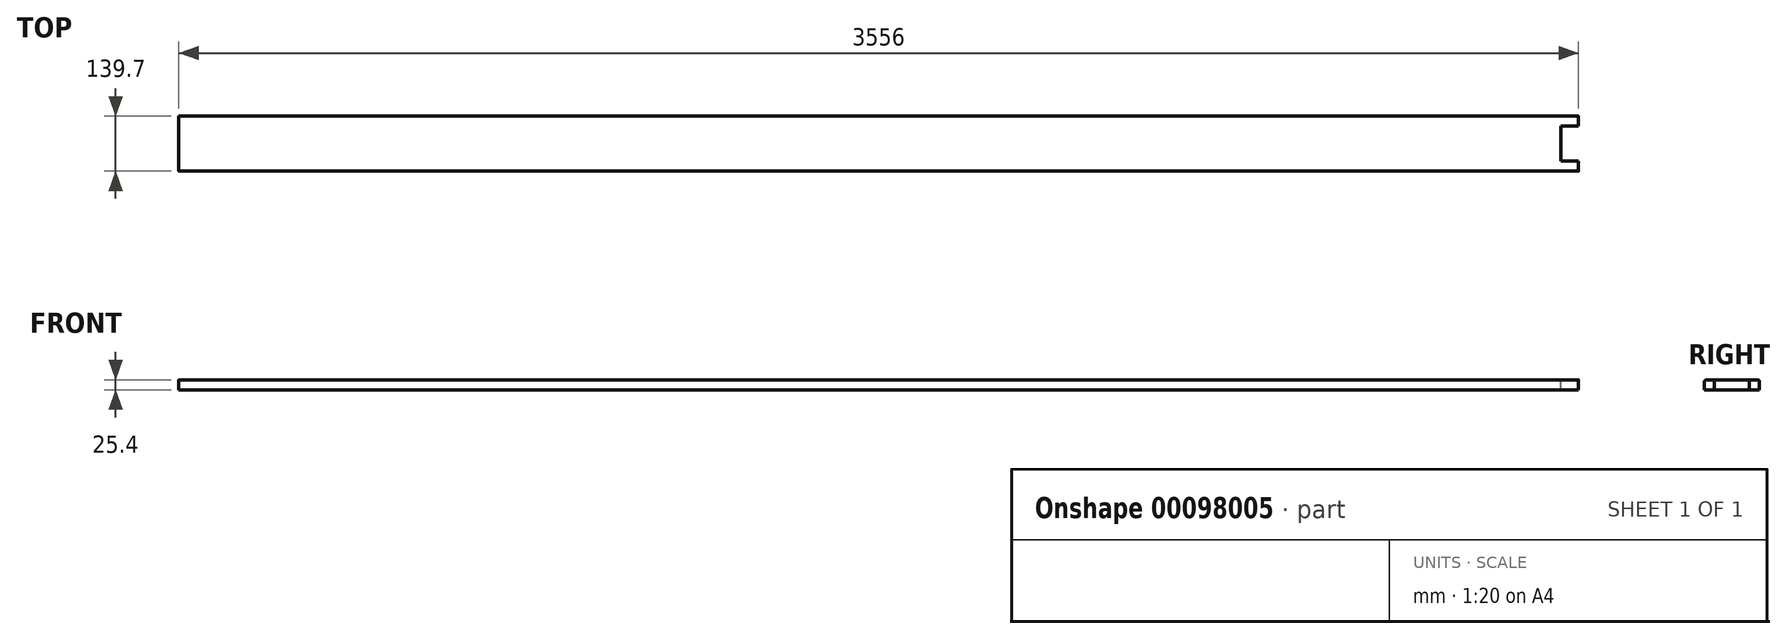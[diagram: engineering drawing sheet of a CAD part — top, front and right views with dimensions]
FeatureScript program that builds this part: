
annotation { "Feature Type Name" : "Feature", "Feature Type Description" : "" }
export const myFeature = defineFeature(function(context is Context, id is Id, definition is map)
    precondition{}
    {
        {
            var Q0;
            Q0=qCreatedBy(makeId("Top.planeOp"),FACE);
            var sketch = newSketch(context, id + "F0", { "sketchPlane" : qUnion([Q0])});
            skLineSegment(sketch, "E0.bottom", {"start": v(1778, 69.85) * mm, "end": v(-1778, 69.85) * mm});
            skLineSegment(sketch, "E0.top", {"start": v(1778, -69.85) * mm, "end": v(-1778, -69.85) * mm});
            skLineSegment(sketch, "E0.left", {"start": v(1778, 69.85) * mm, "end": v(1778, -69.85) * mm});
            skLineSegment(sketch, "E0.right", {"start": v(-1778, 69.85) * mm, "end": v(-1778, -69.85) * mm});
            skPoint(sketch, "E0.middle", {"position": v(0, 0) * mm});
            skSolve(sketch);
        }
        {
            var Q0;
            Q0=makeQuery(id+"F0.imprint","IMPRINT",FACE,{"disambiguationData":[TD([[makeQuery(id+"F0.imprint","IMPRINT",EDGE,{"derivedFrom":sQuery(id+"F0.wireOp",EDGE,"E0.bottom")}),1.0]])]});
            extrude(context, id + "F1", {"entities" : qUnion([Q0]), "depth" : 25.4 * mm});
        }
        {
            var Q0;
            Q0=makeQuery(id+"F1.opExtrude","CAP_FACE",FACE,{"disambiguationData":[OSD([sQuery(id+"F0.wireOp",EDGE,"E0.bottom"),sQuery(id+"F0.wireOp",EDGE,"E0.top"),sQuery(id+"F0.wireOp",EDGE,"E0.left"),sQuery(id+"F0.wireOp",EDGE,"E0.right")])],"isStart":false});
            var sketch = newSketch(context, id + "F2", { "sketchPlane" : qUnion([Q0])});
            skLineSegment(sketch, "E1", {"start": v(1778, 44.45) * mm, "end": v(1733.55, 44.45) * mm});
            skLineSegment(sketch, "E2", {"start": v(1733.55, 44.45) * mm, "end": v(1733.55, -44.45) * mm});
            skLineSegment(sketch, "E3", {"start": v(1733.55, -44.45) * mm, "end": v(1778, -44.45) * mm});
            skLineSegment(sketch, "E4", {"start": v(1778, -44.45) * mm, "end": v(1778, 44.45) * mm});
            skSolve(sketch);
        }
        {
            var Q0;
            Q0 = qSketchRegion(id + "F2", true);
            extrude(context, id + "F3", {"entities" : qUnion([Q0]), "operationType" : NewBodyOperationType.REMOVE, "endBound" : BoundingType.THROUGH_ALL, "oppositeDirection" : true, "depth" : 25.4 * mm});
        }
        {
            var Q0;
            Q0=makeQuery(id+"F1.opExtrude","CAP_EDGE",EDGE,{"disambiguationData":[OSD([sQuery(id+"F0.wireOp",EDGE,"E0.top")])],"isStart":false});
            var Q1;
            Q1=makeQuery(id+"F1.opExtrude","CAP_EDGE",EDGE,{"disambiguationData":[OSD([sQuery(id+"F0.wireOp",EDGE,"E0.bottom")])],"isStart":false});
            fillet(context, id + "F4", {"entities" : qUnion([Q0, Q1]), "radius" : 5.08 * mm, "tangentPropagation" : true, "allowEdgeOverflow" : false});
        }
    });
